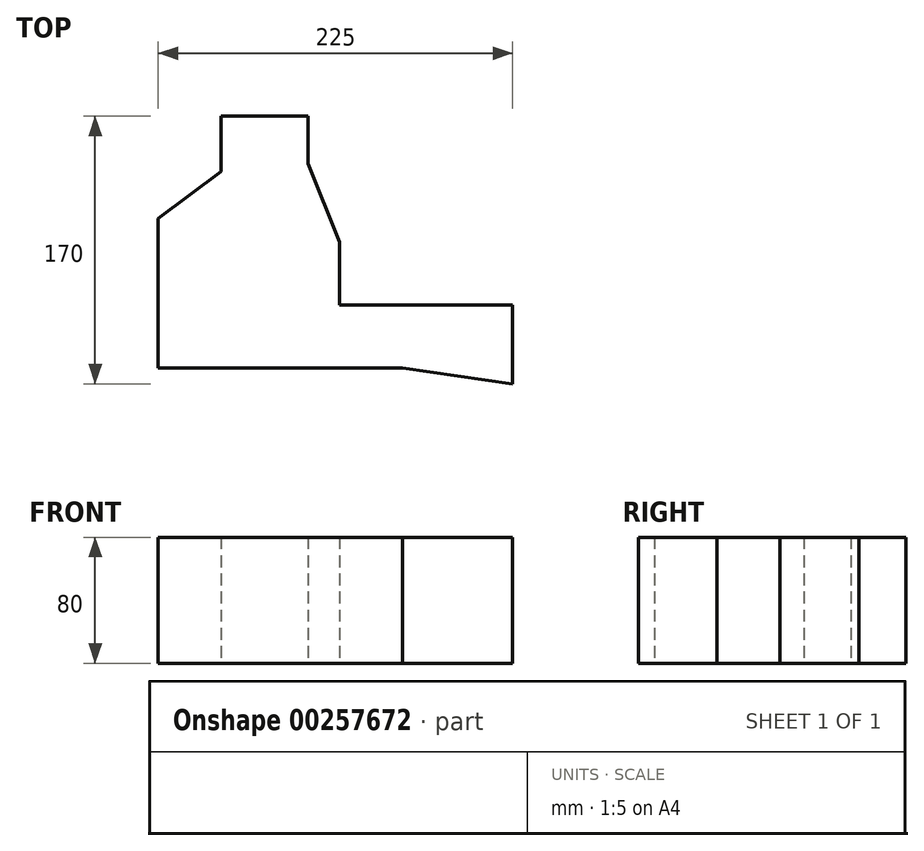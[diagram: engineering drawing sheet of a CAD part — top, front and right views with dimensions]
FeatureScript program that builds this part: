
annotation { "Feature Type Name" : "Feature", "Feature Type Description" : "" }
export const myFeature = defineFeature(function(context is Context, id is Id, definition is map)
    precondition{}
    {
        {
            var Q0;
            Q0=qCreatedBy(makeId("Top.planeOp"),FACE);
            var sketch = newSketch(context, id + "F0", { "sketchPlane" : qUnion([Q0])});
            skLineSegment(sketch, "E0", {"start": v(61.88, -65.37) * mm, "end": v(-93.12, -65.37) * mm});
            skLineSegment(sketch, "E1", {"start": v(-93.12, -65.37) * mm, "end": v(-93.12, 29.63) * mm});
            skLineSegment(sketch, "E2", {"start": v(-53.12, 59.63) * mm, "end": v(-53.12, 94.63) * mm});
            skLineSegment(sketch, "E3", {"start": v(-93.12, 29.63) * mm, "end": v(-53.12, 59.63) * mm});
            skLineSegment(sketch, "E4", {"start": v(-53.12, 94.63) * mm, "end": v(1.88, 94.63) * mm});
            skLineSegment(sketch, "E5", {"start": v(1.88, 94.63) * mm, "end": v(1.88, 64.63) * mm});
            skLineSegment(sketch, "E6", {"start": v(1.88, 64.63) * mm, "end": v(21.88, 14.63) * mm});
            skLineSegment(sketch, "E7", {"start": v(21.88, 14.63) * mm, "end": v(21.88, -25.37) * mm});
            skPoint(sketch, "E8", {"position": v(-93.12, -25.37) * mm});
            skLineSegment(sketch, "E9", {"start": v(21.88, -25.37) * mm, "end": v(131.88, -25.37) * mm});
            skLineSegment(sketch, "E10", {"start": v(131.88, -25.37) * mm, "end": v(131.88, -75.37) * mm});
            skLineSegment(sketch, "E11", {"start": v(61.88, -65.37) * mm, "end": v(131.88, -75.37) * mm});
            skSolve(sketch);
        }
        {
            var Q0;
            Q0=makeQuery(id+"F0.imprint","IMPRINT",FACE,{"disambiguationData":[TD([[makeQuery(id+"F0.imprint","IMPRINT",EDGE,{"derivedFrom":sQuery(id+"F0.wireOp",EDGE,"E0")}),-1.0]])]});
            extrude(context, id + "F1", {"entities" : qUnion([Q0]), "depth" : 80 * mm});
        }
    });
